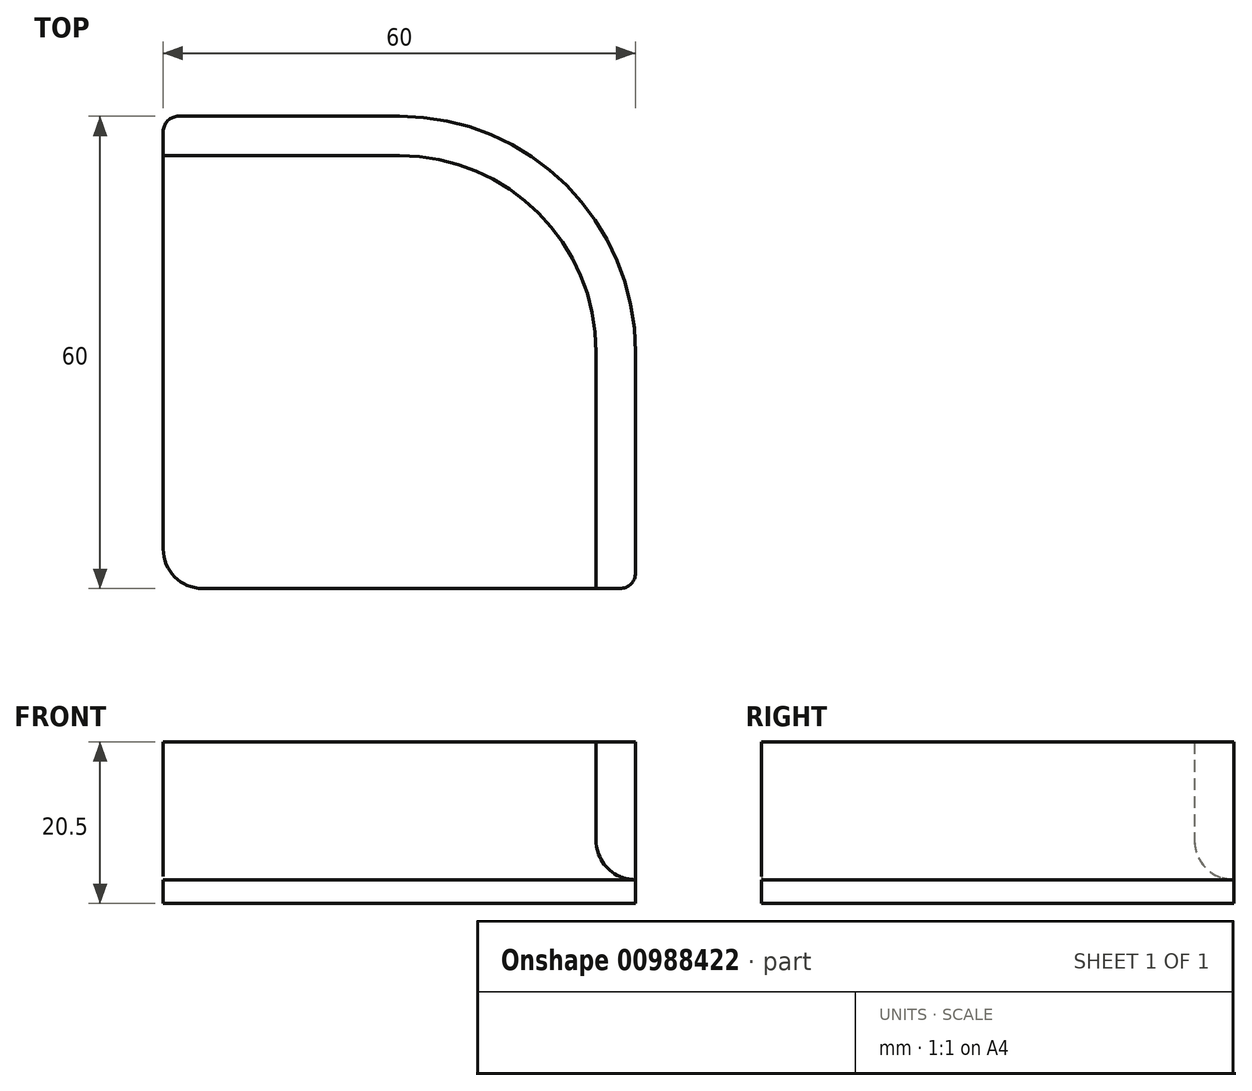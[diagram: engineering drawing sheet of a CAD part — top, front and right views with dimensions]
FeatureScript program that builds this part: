
annotation { "Feature Type Name" : "Feature", "Feature Type Description" : "" }
export const myFeature = defineFeature(function(context is Context, id is Id, definition is map)
    precondition{}
    {
        {
            var Q0;
            Q0=qCreatedBy(makeId("Top.planeOp"),FACE);
            var sketch = newSketch(context, id + "F0", { "sketchPlane" : qUnion([Q0])});
            skLineSegment(sketch, "E0", {"start": v(0, 0) * mm, "end": v(30, 0) * mm});
            skLineSegment(sketch, "E1", {"start": v(60, -30) * mm, "end": v(60, -60) * mm});
            skPoint(sketch, "E2.visualSharp", {"position": v(60, 0) * mm});
            skArc(sketch, "E2.filletArc", {"start": v(60, -30) * mm, "mid": v(51.21, -8.79) * mm, "end": v(30, 0) * mm});
            skLineSegment(sketch, "E3", {"start": v(0, 0) * mm, "end": v(0, -60) * mm});
            skLineSegment(sketch, "E4", {"start": v(0, -60) * mm, "end": v(60, -60) * mm});
            skSolve(sketch);
        }
        {
            var Q0;
            Q0 = qSketchRegion(id + "F0", true);
            extrude(context, id + "F1", {"entities" : qUnion([Q0]), "depth" : 3 * mm, "offsetDistance" : 25 * mm});
        }
        {
            var Q0;
            Q0=makeQuery(id+"F1.opExtrude","CAP_FACE",FACE,{"disambiguationData":[OSD([sQuery(id+"F0.wireOp",EDGE,"E0"),sQuery(id+"F0.wireOp",EDGE,"E1"),sQuery(id+"F0.wireOp",EDGE,"E2.filletArc"),sQuery(id+"F0.wireOp",EDGE,"E3"),sQuery(id+"F0.wireOp",EDGE,"E4")])],"isStart":false});
            var sketch = newSketch(context, id + "F2", { "sketchPlane" : qUnion([Q0])});
            skLineSegment(sketch, "E5.0", {"start": v(0, 0) * mm, "end": v(30, 0) * mm});
            skArc(sketch, "E6.0", {"start": v(60, -30) * mm, "mid": v(51.21, -8.79) * mm, "end": v(30, 0) * mm});
            skLineSegment(sketch, "E7.0", {"start": v(60, -30) * mm, "end": v(60, -60) * mm});
            skLineSegment(sketch, "E8.0", {"start": v(55, -30) * mm, "end": v(55, -60) * mm});
            skArc(sketch, "E8.1", {"start": v(55, -30) * mm, "mid": v(47.68, -12.32) * mm, "end": v(30, -5) * mm});
            skLineSegment(sketch, "E8.2", {"start": v(0, -5) * mm, "end": v(30, -5) * mm});
            skLineSegment(sketch, "E9", {"start": v(55, -60) * mm, "end": v(60, -60) * mm});
            skLineSegment(sketch, "E10", {"start": v(0, 0) * mm, "end": v(0, -5) * mm});
            skSolve(sketch);
        }
        {
            var Q0;
            Q0=makeQuery(id+"F2.imprint","IMPRINT",FACE,{"disambiguationData":[TD([[makeQuery(id+"F2.imprint","IMPRINT",EDGE,{"derivedFrom":sQuery(id+"F2.wireOp",EDGE,"E6.0")}),1.0]])]});
            extrude(context, id + "F3", {"entities" : qUnion([Q0]), "depth" : 17.5 * mm, "offsetDistance" : 25 * mm});
        }
        {
            var Q0;
            Q0=makeQuery(id+"F1.opExtrude","SWEPT_EDGE",EDGE,{"disambiguationData":[OSD([sQuery(id+"F0.wireOp",EDGE,"E3"),sQuery(id+"F0.wireOp",EDGE,"E4")])]});
            fillet(context, id + "F4", {"entities" : qUnion([Q0]), "radius" : 5 * mm, "tangentPropagation" : true, "allowEdgeOverflow" : false});
        }
        {
            var Q0;
            Q0=makeQuery(id+"F1.opExtrude","SWEPT_EDGE",EDGE,{"disambiguationData":[OSD([sQuery(id+"F0.wireOp",EDGE,"E0"),sQuery(id+"F0.wireOp",EDGE,"E3")])]});
            var Q1;
            Q1=makeQuery(id+"F3.opExtrude","SWEPT_EDGE",EDGE,{"disambiguationData":[OSD([sQuery(id+"F2.wireOp",EDGE,"E5.0"),sQuery(id+"F2.wireOp",EDGE,"E10")])]});
            fillet(context, id + "F5", {"entities" : qUnion([Q0, Q1]), "radius" : 2 * mm, "tangentPropagation" : true, "allowEdgeOverflow" : false});
        }
        {
            var Q0;
            Q0=makeQuery(id+"F1.opExtrude","SWEPT_EDGE",EDGE,{"disambiguationData":[OSD([sQuery(id+"F0.wireOp",EDGE,"E1"),sQuery(id+"F0.wireOp",EDGE,"E4")])]});
            var Q1;
            Q1=makeQuery(id+"F3.opExtrude","SWEPT_EDGE",EDGE,{"disambiguationData":[OSD([sQuery(id+"F2.wireOp",EDGE,"E7.0"),sQuery(id+"F2.wireOp",EDGE,"E9")])]});
            fillet(context, id + "F6", {"entities" : qUnion([Q0, Q1]), "radius" : 2 * mm, "tangentPropagation" : true, "allowEdgeOverflow" : false});
        }
        {
            var Q0;
            Q0=makeQuery(id+"F3.opExtrude","CAP_EDGE",EDGE,{"disambiguationData":[OSD([sQuery(id+"F2.wireOp",EDGE,"E8.2")])],"isStart":true});
            var Q1;
            Q1=makeQuery(id+"F3.opExtrude","CAP_EDGE",EDGE,{"disambiguationData":[OSD([sQuery(id+"F2.wireOp",EDGE,"E8.1")])],"isStart":true});
            var Q2;
            Q2=makeQuery(id+"F3.opExtrude","CAP_EDGE",EDGE,{"disambiguationData":[OSD([sQuery(id+"F2.wireOp",EDGE,"E8.0")])],"isStart":true});
            fillet(context, id + "F7", {"entities" : qUnion([Q0, Q1, Q2]), "radius" : 5 * mm, "tangentPropagation" : true, "allowEdgeOverflow" : false});
        }
    });
